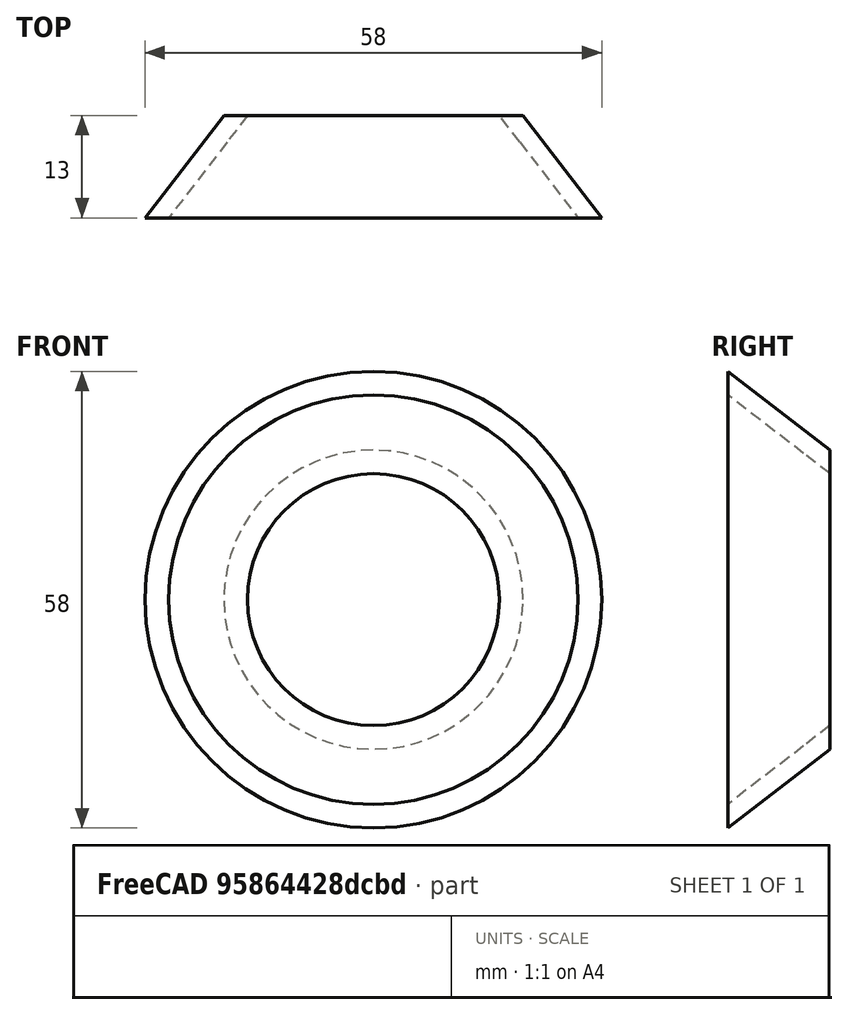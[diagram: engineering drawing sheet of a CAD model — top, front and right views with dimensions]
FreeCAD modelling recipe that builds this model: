
FCSTD DOCUMENT  (FreeCAD 0.18R16131 (Git))
Label: S200_cone2
License: All rights reserved
LicenseURL: http://en.wikipedia.org/wiki/All_rights_reserved
objects: Sketcher::SketchObject×1, PartDesign::Revolution×1, PartDesign::Body×1
note: 4 computed .brp shape members not serialized (recipe doc carries the construction recipe); baked Part::Feature solids carry a one-line shape summary decoded from their .brp

FEATURE [Sketcher::SketchObject] Sketch
  MapMode = 5
  Support = -> [XY_Plane]
  sketch-geometry (5):
    g0: LineSegment StartX=26 StartY=0.00243201 StartZ=0 EndX=29 EndY=0.00243201 EndZ=0
    g1: LineSegment StartX=16 StartY=13 StartZ=0 EndX=19 EndY=13 EndZ=0
    g2: LineSegment StartX=19 StartY=13 StartZ=0 EndX=29 EndY=0.00243201 EndZ=0
    g3: LineSegment StartX=18.5865 StartY=9.63813 StartZ=0 EndX=26 EndY=0.00243201 EndZ=0
    g4: LineSegment StartX=18.5865 StartY=9.63813 StartZ=0 EndX=16 EndY=13 EndZ=0
  constraints (13):
    c: Horizontal(g0)
    c: Horizontal(g1)
    c: Coincident(g2,g1)
    c: Coincident(g2,g0)
    c: Parallel(g3,g2)
    c: Coincident(g0,g3)
    c: Distance(g0) = 3
    c: Distance(g-1,g0) = 29
    c: Coincident(g4,g3)
    c: Parallel(g4,g3)
    c: Coincident(g1,g4)
    c: DistanceX(g-1,g1) = 19
    c: DistanceY(g-1,g1) = 13
FEATURE [PartDesign::Revolution] Revolution
  Angle = 360
  Axis = (1e-16,1,-1e-16)
  Base = (0,0,0)
  Profile = -> Sketch
  ReferenceAxis = -> Y_Axis
  Reversed = true
FEATURE [PartDesign::Body] Body
  Group = -> [Sketch,Revolution]
  Origin = -> Origin
  Tip = -> Revolution
